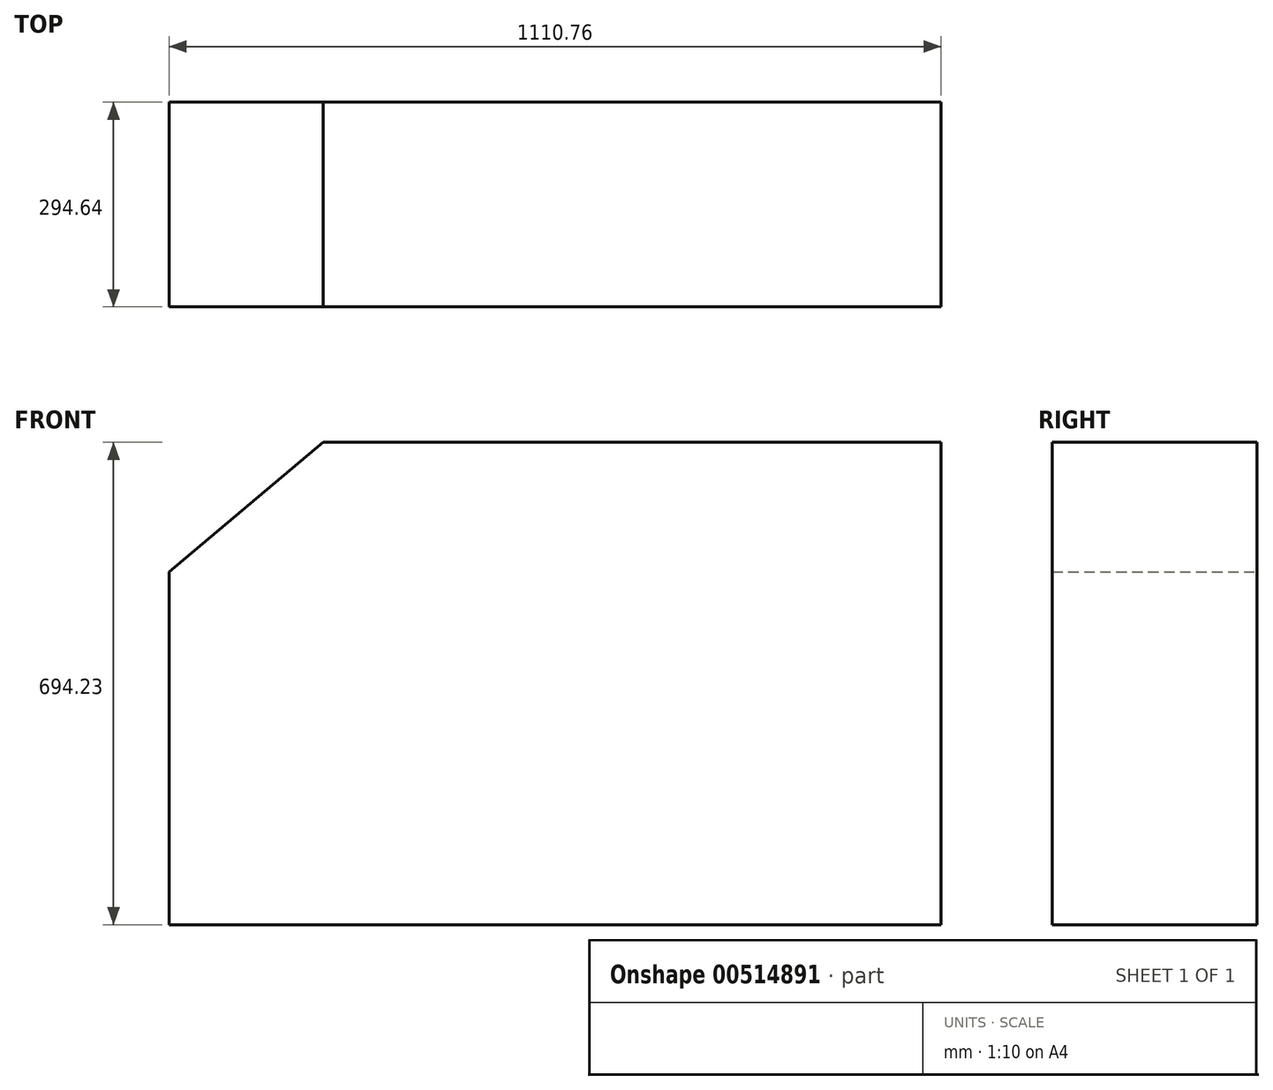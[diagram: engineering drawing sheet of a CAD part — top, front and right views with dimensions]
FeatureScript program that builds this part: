
annotation { "Feature Type Name" : "Feature", "Feature Type Description" : "" }
export const myFeature = defineFeature(function(context is Context, id is Id, definition is map)
    precondition{}
    {
        {
            var Q0;
            Q0=qCreatedBy(makeId("Front.planeOp"),FACE);
            var sketch = newSketch(context, id + "F0", { "sketchPlane" : qUnion([Q0])});
            skLineSegment(sketch, "E0", {"start": v(0, 0) * mm, "end": v(0, 694.23) * mm});
            skLineSegment(sketch, "E1", {"start": v(0, 694.23) * mm, "end": v(-889, 694.23) * mm});
            skLineSegment(sketch, "E2", {"start": v(-1110.76, 508) * mm, "end": v(-1110.76, 0) * mm});
            skLineSegment(sketch, "E3", {"start": v(-1110.76, 0) * mm, "end": v(0, 0) * mm});
            skLineSegment(sketch, "E4", {"start": v(-1110.76, 508) * mm, "end": v(-889, 694.23) * mm});
            skSolve(sketch);
        }
        {
            var Q0;
            Q0 = qSketchRegion(id + "F0", true);
            extrude(context, id + "F1", {"entities" : qUnion([Q0]), "depth" : 294.64 * mm, "offsetDistance" : 25.4 * mm});
        }
    });
